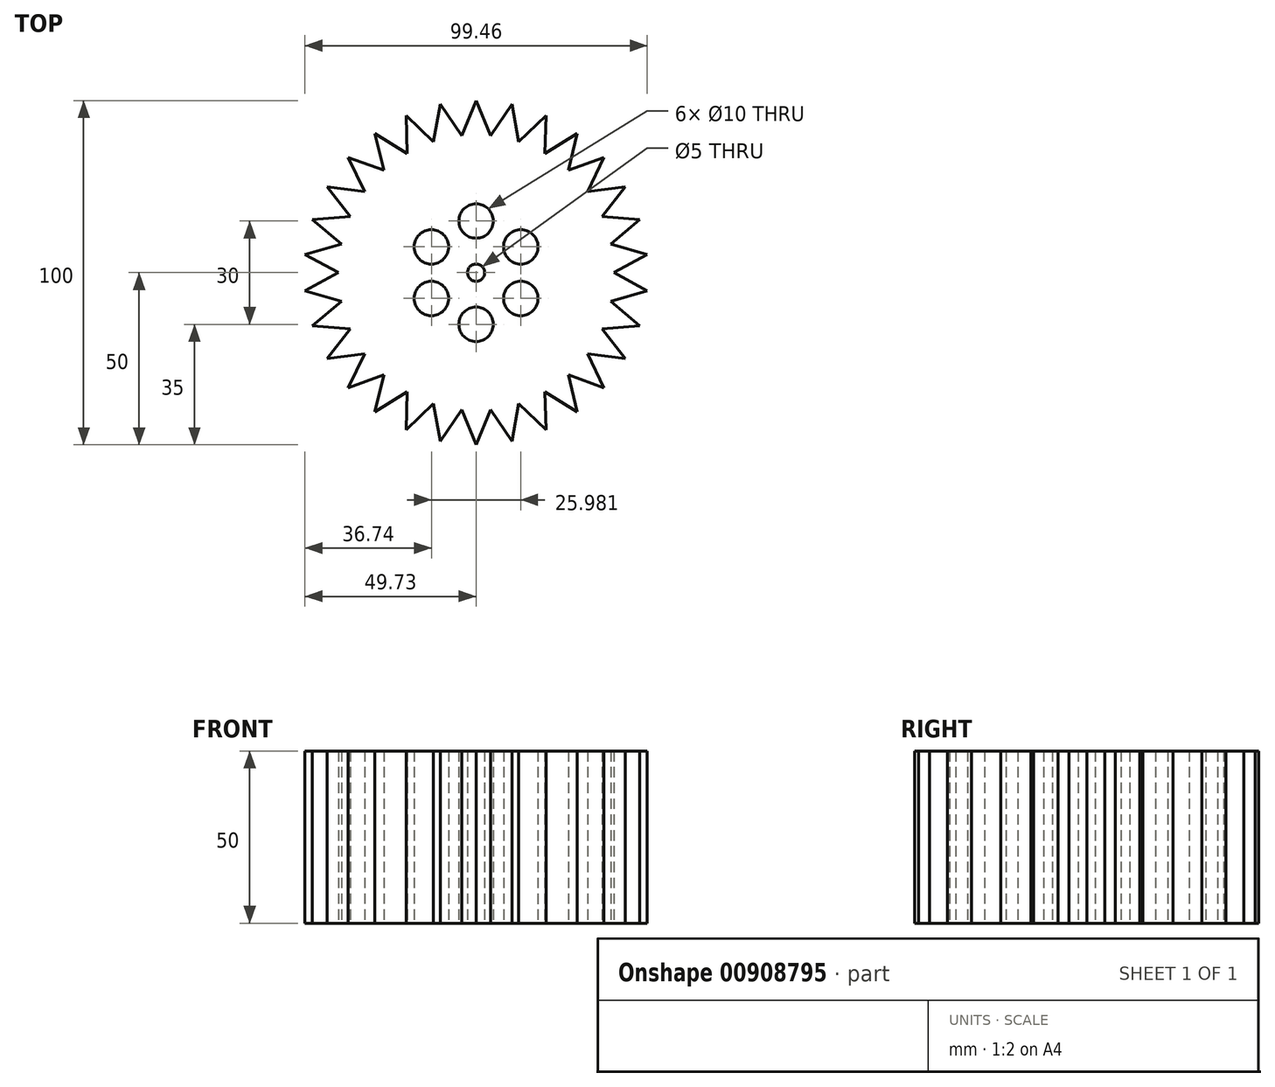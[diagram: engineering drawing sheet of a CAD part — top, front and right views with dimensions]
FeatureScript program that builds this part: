
annotation { "Feature Type Name" : "Feature", "Feature Type Description" : "" }
export const myFeature = defineFeature(function(context is Context, id is Id, definition is map)
    precondition{}
    {
        {
            var Q0;
            Q0=qCreatedBy(makeId("Top.planeOp"),FACE);
            var sketch = newSketch(context, id + "F0", { "sketchPlane" : qUnion([Q0])});
            skCircle(sketch, "E0", {"center": v(0, 0) * mm, "radius": 50 * mm});
            skLineSegment(sketch, "E1", {"start": v(-4.18, 39.78) * mm, "end": v(-10.4, 48.9) * mm});
            skLineSegment(sketch, "E2", {"start": v(-4.18, 39.78) * mm, "end": v(0, 50) * mm});
            skLineSegment(sketch, "E3.1.0", {"start": v(-12.36, 38.04) * mm, "end": v(-20.34, 45.68) * mm});
            skLineSegment(sketch, "E3.2.0", {"start": v(-20, 34.64) * mm, "end": v(-29.39, 40.45) * mm});
            skLineSegment(sketch, "E3.3.0", {"start": v(-26.77, 29.73) * mm, "end": v(-37.16, 33.46) * mm});
            skLineSegment(sketch, "E3.4.0", {"start": v(-32.36, 23.51) * mm, "end": v(-43.3, 25) * mm});
            skLineSegment(sketch, "E3.5.0", {"start": v(-36.54, 16.27) * mm, "end": v(-47.55, 15.45) * mm});
            skLineSegment(sketch, "E3.6.0", {"start": v(-39.13, 8.32) * mm, "end": v(-49.73, 5.23) * mm});
            skLineSegment(sketch, "E3.7.0", {"start": v(-40, 0) * mm, "end": v(-49.73, -5.23) * mm});
            skLineSegment(sketch, "E3.8.0", {"start": v(-39.13, -8.32) * mm, "end": v(-47.55, -15.45) * mm});
            skLineSegment(sketch, "E3.9.0", {"start": v(-36.54, -16.27) * mm, "end": v(-43.3, -25) * mm});
            skLineSegment(sketch, "E3.10.0", {"start": v(-32.36, -23.51) * mm, "end": v(-37.16, -33.46) * mm});
            skLineSegment(sketch, "E3.11.0", {"start": v(-26.77, -29.73) * mm, "end": v(-29.39, -40.45) * mm});
            skLineSegment(sketch, "E3.12.0", {"start": v(-20, -34.64) * mm, "end": v(-20.34, -45.68) * mm});
            skLineSegment(sketch, "E3.13.0", {"start": v(-12.36, -38.04) * mm, "end": v(-10.4, -48.9) * mm});
            skLineSegment(sketch, "E3.14.0", {"start": v(-4.18, -39.78) * mm, "end": v(0, -50) * mm});
            skLineSegment(sketch, "E3.15.0", {"start": v(4.18, -39.78) * mm, "end": v(10.4, -48.9) * mm});
            skLineSegment(sketch, "E3.16.0", {"start": v(12.36, -38.04) * mm, "end": v(20.34, -45.68) * mm});
            skLineSegment(sketch, "E3.17.0", {"start": v(20, -34.64) * mm, "end": v(29.39, -40.45) * mm});
            skLineSegment(sketch, "E3.18.0", {"start": v(26.77, -29.73) * mm, "end": v(37.16, -33.46) * mm});
            skLineSegment(sketch, "E3.19.0", {"start": v(32.36, -23.51) * mm, "end": v(43.3, -25) * mm});
            skLineSegment(sketch, "E3.20.0", {"start": v(36.54, -16.27) * mm, "end": v(47.55, -15.45) * mm});
            skLineSegment(sketch, "E3.21.0", {"start": v(39.13, -8.32) * mm, "end": v(49.73, -5.23) * mm});
            skLineSegment(sketch, "E3.22.0", {"start": v(40, 0) * mm, "end": v(49.73, 5.23) * mm});
            skLineSegment(sketch, "E3.23.0", {"start": v(39.13, 8.32) * mm, "end": v(47.55, 15.45) * mm});
            skLineSegment(sketch, "E3.24.0", {"start": v(36.54, 16.27) * mm, "end": v(43.3, 25) * mm});
            skLineSegment(sketch, "E3.25.0", {"start": v(32.36, 23.51) * mm, "end": v(37.16, 33.46) * mm});
            skLineSegment(sketch, "E3.26.0", {"start": v(26.77, 29.73) * mm, "end": v(29.39, 40.45) * mm});
            skLineSegment(sketch, "E3.27.0", {"start": v(20, 34.64) * mm, "end": v(20.34, 45.68) * mm});
            skLineSegment(sketch, "E3.28.0", {"start": v(12.36, 38.04) * mm, "end": v(10.4, 48.9) * mm});
            skLineSegment(sketch, "E3.29.0", {"start": v(4.18, 39.78) * mm, "end": v(0, 50) * mm});
            skLineSegment(sketch, "E4.1.0", {"start": v(-12.36, 38.04) * mm, "end": v(-10.4, 48.9) * mm});
            skLineSegment(sketch, "E4.2.0", {"start": v(-20, 34.64) * mm, "end": v(-20.34, 45.68) * mm});
            skLineSegment(sketch, "E5.1.3.0", {"start": v(-26.77, 29.73) * mm, "end": v(-29.39, 40.45) * mm});
            skLineSegment(sketch, "E5.1.4.0", {"start": v(-32.36, 23.51) * mm, "end": v(-37.16, 33.46) * mm});
            skLineSegment(sketch, "E5.1.5.0", {"start": v(-36.54, 16.27) * mm, "end": v(-43.3, 25) * mm});
            skLineSegment(sketch, "E5.1.6.0", {"start": v(-39.13, 8.32) * mm, "end": v(-47.55, 15.45) * mm});
            skLineSegment(sketch, "E5.1.7.0", {"start": v(-40, 0) * mm, "end": v(-49.73, 5.23) * mm});
            skLineSegment(sketch, "E5.1.8.0", {"start": v(-39.13, -8.32) * mm, "end": v(-49.73, -5.23) * mm});
            skLineSegment(sketch, "E5.1.9.0", {"start": v(-36.54, -16.27) * mm, "end": v(-47.55, -15.45) * mm});
            skLineSegment(sketch, "E5.1.10.0", {"start": v(-32.36, -23.51) * mm, "end": v(-43.3, -25) * mm});
            skLineSegment(sketch, "E5.1.11.0", {"start": v(-26.77, -29.73) * mm, "end": v(-37.16, -33.46) * mm});
            skLineSegment(sketch, "E5.1.12.0", {"start": v(-20, -34.64) * mm, "end": v(-29.39, -40.45) * mm});
            skLineSegment(sketch, "E5.1.13.0", {"start": v(-12.36, -38.04) * mm, "end": v(-20.34, -45.68) * mm});
            skLineSegment(sketch, "E5.1.14.0", {"start": v(-4.18, -39.78) * mm, "end": v(-10.4, -48.9) * mm});
            skLineSegment(sketch, "E5.1.15.0", {"start": v(4.18, -39.78) * mm, "end": v(0, -50) * mm});
            skLineSegment(sketch, "E5.1.16.0", {"start": v(12.36, -38.04) * mm, "end": v(10.4, -48.9) * mm});
            skLineSegment(sketch, "E5.1.17.0", {"start": v(20, -34.64) * mm, "end": v(20.34, -45.68) * mm});
            skLineSegment(sketch, "E5.1.18.0", {"start": v(26.77, -29.73) * mm, "end": v(29.39, -40.45) * mm});
            skLineSegment(sketch, "E5.1.19.0", {"start": v(32.36, -23.51) * mm, "end": v(37.16, -33.46) * mm});
            skLineSegment(sketch, "E5.1.20.0", {"start": v(36.54, -16.27) * mm, "end": v(43.3, -25) * mm});
            skLineSegment(sketch, "E5.1.21.0", {"start": v(39.13, -8.32) * mm, "end": v(47.55, -15.45) * mm});
            skLineSegment(sketch, "E5.1.22.0", {"start": v(40, 0) * mm, "end": v(49.73, -5.23) * mm});
            skLineSegment(sketch, "E5.1.23.0", {"start": v(39.13, 8.32) * mm, "end": v(49.73, 5.23) * mm});
            skLineSegment(sketch, "E5.1.24.0", {"start": v(36.54, 16.27) * mm, "end": v(47.55, 15.45) * mm});
            skLineSegment(sketch, "E5.1.25.0", {"start": v(32.36, 23.51) * mm, "end": v(43.3, 25) * mm});
            skLineSegment(sketch, "E5.1.26.0", {"start": v(26.77, 29.73) * mm, "end": v(37.16, 33.46) * mm});
            skLineSegment(sketch, "E5.1.27.0", {"start": v(20, 34.64) * mm, "end": v(29.39, 40.45) * mm});
            skLineSegment(sketch, "E5.1.28.0", {"start": v(12.36, 38.04) * mm, "end": v(20.34, 45.68) * mm});
            skLineSegment(sketch, "E5.1.29.0", {"start": v(4.18, 39.78) * mm, "end": v(10.4, 48.9) * mm});
            skCircle(sketch, "E6", {"center": v(0, 15) * mm, "radius": 5 * mm});
            skCircle(sketch, "E7.1.0", {"center": v(-13, 7.5) * mm, "radius": 5 * mm});
            skCircle(sketch, "E7.2.0", {"center": v(-13, -7.5) * mm, "radius": 5 * mm});
            skCircle(sketch, "E7.3.0", {"center": v(0, -15) * mm, "radius": 5 * mm});
            skCircle(sketch, "E7.4.0", {"center": v(13, -7.5) * mm, "radius": 5 * mm});
            skCircle(sketch, "E7.5.0", {"center": v(13, 7.5) * mm, "radius": 5 * mm});
            skCircle(sketch, "E8", {"center": v(0, 0) * mm, "radius": 2.5 * mm});
            skSolve(sketch);
        }
        {
            var Q0;
            Q0=makeQuery(id+"F0.imprint","IMPRINT",FACE,{"disambiguationData":[TD([[makeQuery(id+"F0.imprint","IMPRINT",EDGE,{"derivedFrom":sQuery(id+"F0.wireOp",EDGE,"E1")}),1.0]])]});
            extrude(context, id + "F1", {"entities" : qUnion([Q0]), "depth" : 50 * mm, "offsetDistance" : 25 * mm});
        }
    });
